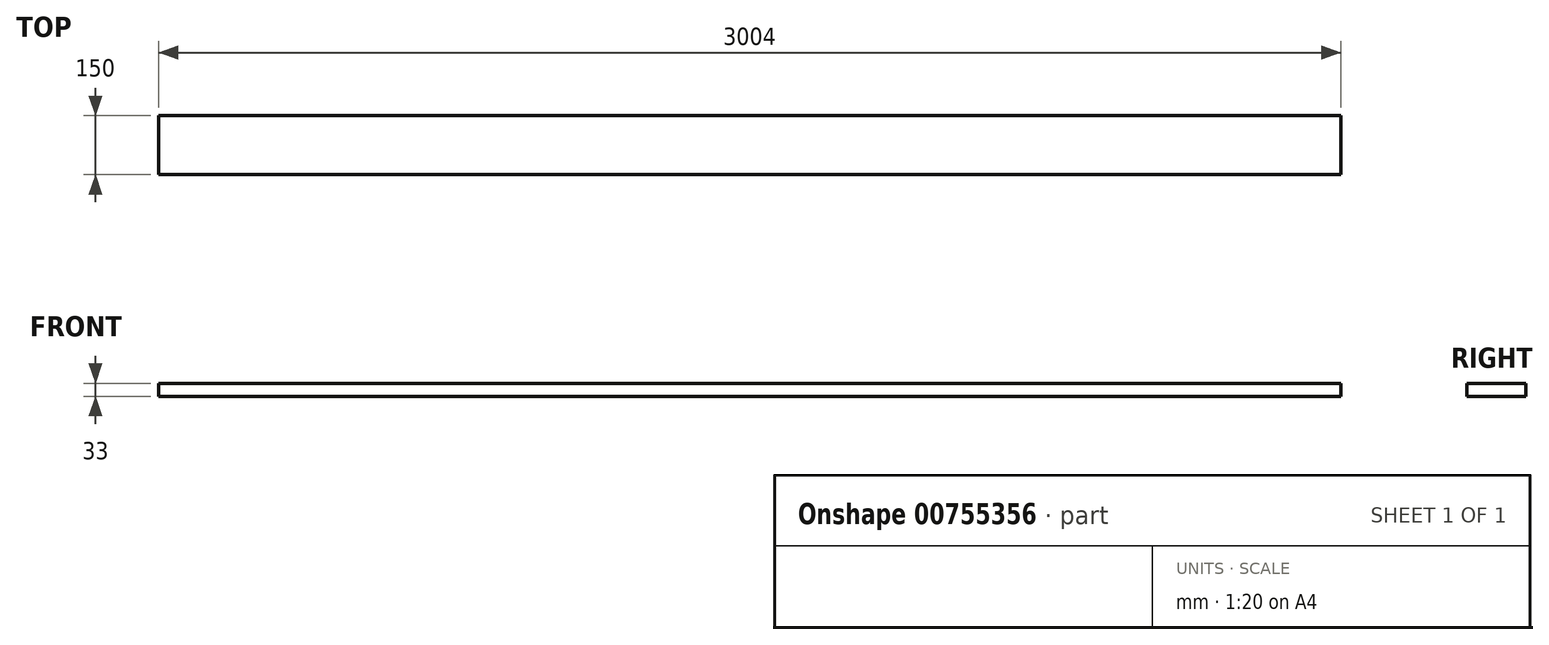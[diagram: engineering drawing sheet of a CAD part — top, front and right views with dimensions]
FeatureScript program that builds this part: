
annotation { "Feature Type Name" : "Feature", "Feature Type Description" : "" }
export const myFeature = defineFeature(function(context is Context, id is Id, definition is map)
    precondition{}
    {
        {
            var Q0;
            Q0=qCreatedBy(makeId("Right.planeOp"),FACE);
            var sketch = newSketch(context, id + "F0", { "sketchPlane" : qUnion([Q0])});
            skLineSegment(sketch, "E0.bottom", {"start": v(75, 16.5) * mm, "end": v(-75, 16.5) * mm});
            skLineSegment(sketch, "E0.top", {"start": v(75, -16.5) * mm, "end": v(-75, -16.5) * mm});
            skLineSegment(sketch, "E0.left", {"start": v(75, 16.5) * mm, "end": v(75, -16.5) * mm});
            skLineSegment(sketch, "E0.right", {"start": v(-75, 16.5) * mm, "end": v(-75, -16.5) * mm});
            skPoint(sketch, "E0.middle", {"position": v(0, 0) * mm});
            skSolve(sketch);
        }
        {
            var Q0;
            Q0=qSketchRegion(id+"F0",true);
            extrude(context, id + "F1", {"entities" : qUnion([Q0]), "endBound" : BoundingType.SYMMETRIC, "depth" : 3004 * mm, "offsetDistance" : 25 * mm});
        }
    });
